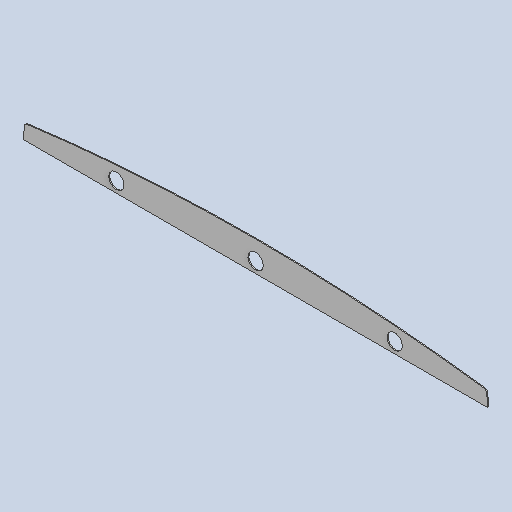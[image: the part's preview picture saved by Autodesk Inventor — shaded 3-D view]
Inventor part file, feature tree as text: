
AUTODESK INVENTOR PART (.ipt)
format: ipt  version: 2025 (Build 290162010, 162A)  size: 207,872 bytes
history: native  units: mm
features: other x3, sheet_metal_op x1, mirror x1, sketch x1
ambient origin geometry x8: Origin, YZ Plane, XZ Plane, XY Plane, X Axis, Y Axis, Z Axis, Center Point
bodies: Body1 (feature_tree)
feature tree (6):
  sheet_metal_op  "Face1"
  mirror  "Mirror3"
  other  "Corner Chamfer2"
  sketch  "Sketch1"  dims[d54=1500.0mm d55=2700.0mm d58=2100.0mm d65=6.0mm d66=6.0mm d68=6.0mm d69=3.0mm d70=3.0mm d75=3.0mm d78=3.0mm d80=3.0mm d83=6.0mm d86=3.0mm d112=251.771mm d113=50.0mm d114=50.0mm d115=3.0mm d117=110.0mm d118=25.0mm d119=122.6mm d120=25.0mm d121=50.0mm d122=50.0mm d123=450.0mm d124=35.0mm d125=3.0mm d126=98.5mm d127=5.0mm d128=5.0mm d132=0.2mm d133=0.2mm d134=2.0mm d135=6.0mm d136=45.0deg]
  other  "Plate3"
  other  "Definition1"
